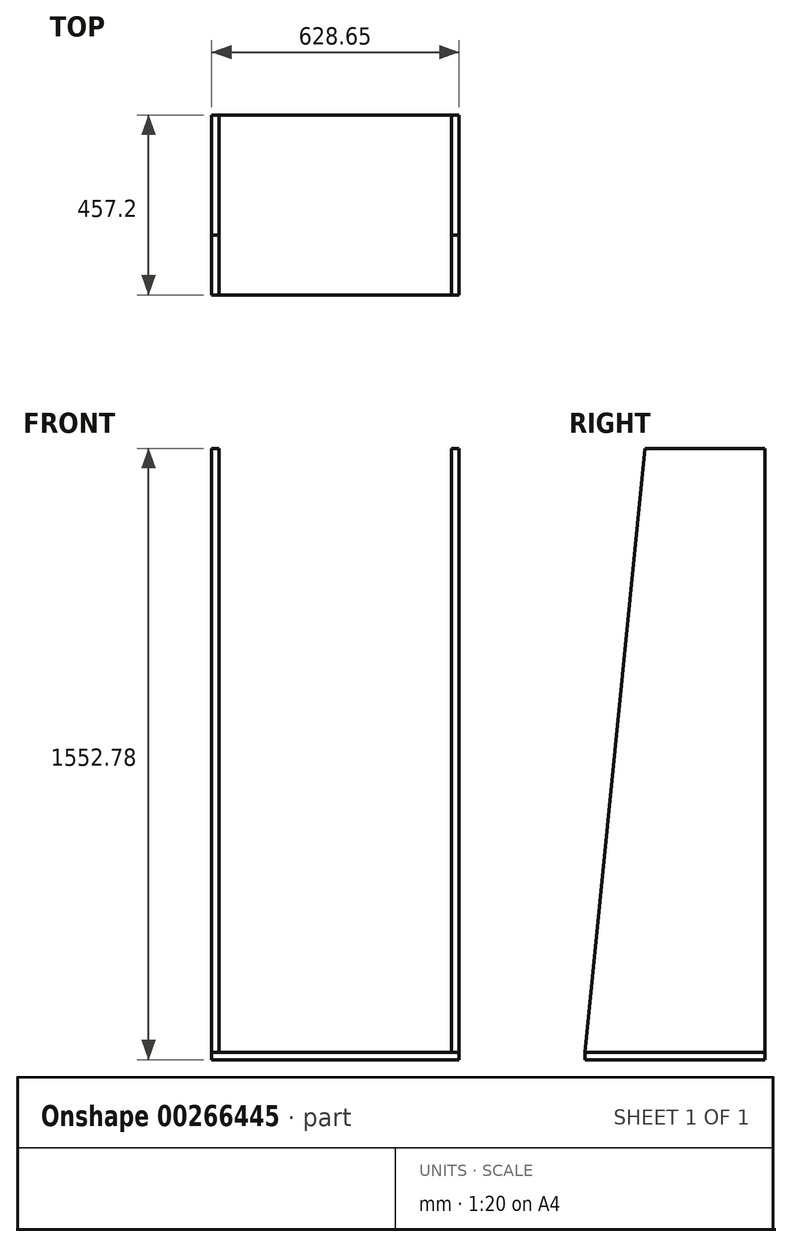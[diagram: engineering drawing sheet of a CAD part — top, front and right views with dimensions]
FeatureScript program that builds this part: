
annotation { "Feature Type Name" : "Feature", "Feature Type Description" : "" }
export const myFeature = defineFeature(function(context is Context, id is Id, definition is map)
    precondition{}
    {
        {
            var Q0;
            Q0=qCreatedBy(makeId("Right.planeOp"),FACE);
            var sketch = newSketch(context, id + "F0", { "sketchPlane" : qUnion([Q0])});
            skLineSegment(sketch, "E0.bottom", {"start": v(0, 0) * mm, "end": v(457.2, 0) * mm});
            skLineSegment(sketch, "E0.top", {"start": v(152.4, 1533.73) * mm, "end": v(457.2, 1533.73) * mm});
            skLineSegment(sketch, "E0.right", {"start": v(457.2, 0) * mm, "end": v(457.2, 1533.73) * mm});
            skLineSegment(sketch, "E1", {"start": v(0, 0) * mm, "end": v(152.4, 1533.73) * mm});
            skSolve(sketch);
        }
        {
            var Q0;
            Q0=makeQuery(id+"F0.imprint","IMPRINT",FACE,{"disambiguationData":[TD([[makeQuery(id+"F0.imprint","IMPRINT",EDGE,{"derivedFrom":sQuery(id+"F0.wireOp",EDGE,"E0.bottom")}),1.0]])]});
            extrude(context, id + "F1", {"entities" : qUnion([Q0]), "depth" : 19.05 * mm});
        }
        {
            var Q0;
            Q0=makeQuery(id+"F1.opExtrude","SWEPT_BODY",BODY,{"disambiguationData":[OSD([sQuery(id+"F0.wireOp",EDGE,"E0.bottom"),sQuery(id+"F0.wireOp",EDGE,"E0.top"),sQuery(id+"F0.wireOp",EDGE,"E0.right"),sQuery(id+"F0.wireOp",EDGE,"E1")])]});
            transform(context, id + "F2", {"entities" : qUnion([Q0]), "transformType" : TransformType.TRANSLATION_3D, "dx" : 609.6 * mm, "dy" : 0 * mm, "dz" : 0 * mm, "makeCopy" : true});
        }
        {
            var Q0;
            Q0=qCreatedBy(makeId("Top.planeOp"),FACE);
            var sketch = newSketch(context, id + "F3", { "sketchPlane" : qUnion([Q0])});
            skLineSegment(sketch, "E2.bottom", {"start": v(0, 0) * mm, "end": v(628.65, 0) * mm});
            skLineSegment(sketch, "E2.top", {"start": v(0, 457.2) * mm, "end": v(628.65, 457.2) * mm});
            skLineSegment(sketch, "E2.left", {"start": v(0, 0) * mm, "end": v(0, 457.2) * mm});
            skLineSegment(sketch, "E2.right", {"start": v(628.65, 0) * mm, "end": v(628.65, 457.2) * mm});
            skSolve(sketch);
        }
        {
            var Q0;
            Q0=makeQuery(id+"F3.imprint","IMPRINT",FACE,{"disambiguationData":[TD([[makeQuery(id+"F3.imprint","IMPRINT",EDGE,{"derivedFrom":sQuery(id+"F3.wireOp",EDGE,"E2.bottom")}),1.0]])]});
            extrude(context, id + "F4", {"entities" : qUnion([Q0]), "oppositeDirection" : true, "depth" : 19.05 * mm});
        }
    });
